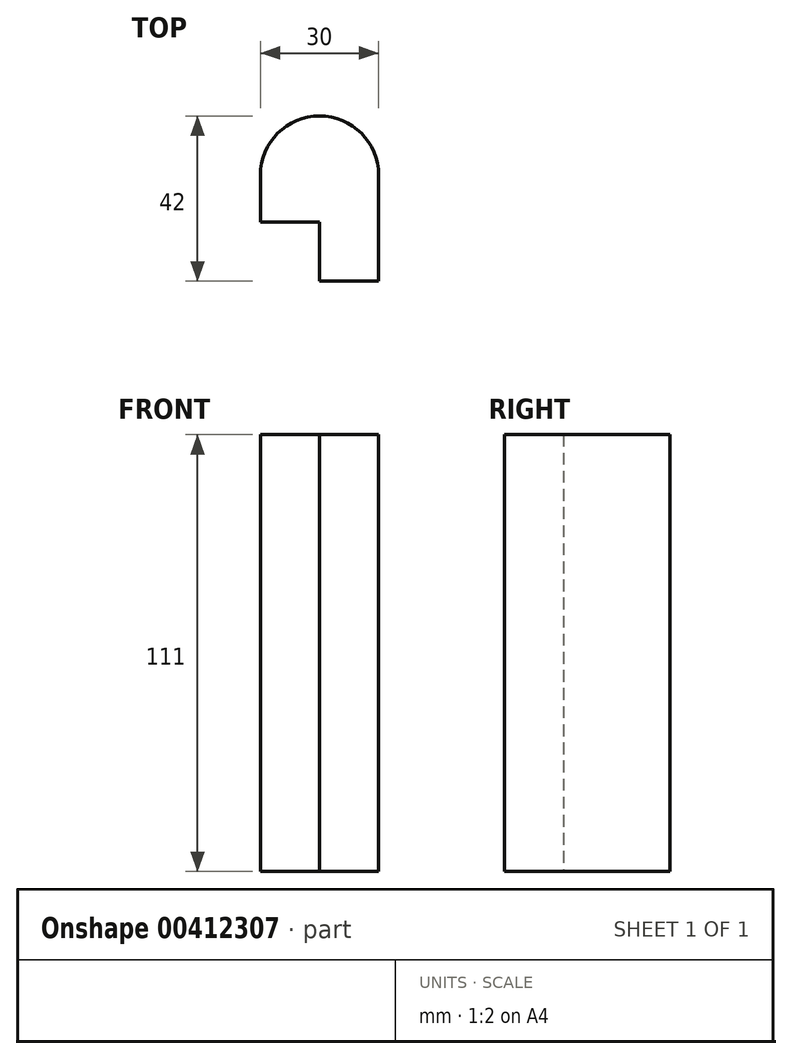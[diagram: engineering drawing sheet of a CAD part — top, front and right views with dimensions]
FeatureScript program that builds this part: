
annotation { "Feature Type Name" : "Feature", "Feature Type Description" : "" }
export const myFeature = defineFeature(function(context is Context, id is Id, definition is map)
    precondition{}
    {
        {
            var Q0;
            Q0=qCreatedBy(makeId("Top.planeOp"),FACE);
            var sketch = newSketch(context, id + "F0", { "sketchPlane" : qUnion([Q0])});
            skLineSegment(sketch, "E0", {"start": v(6.17, 0) * mm, "end": v(6.17, 15) * mm});
            skLineSegment(sketch, "E1", {"start": v(6.17, 15) * mm, "end": v(-8.83, 15) * mm});
            skLineSegment(sketch, "E2", {"start": v(-8.83, 15) * mm, "end": v(-8.83, 27) * mm});
            skLineSegment(sketch, "E3", {"start": v(-8.83, 27) * mm, "end": v(21.17, 27) * mm});
            skLineSegment(sketch, "E4", {"start": v(21.17, 27) * mm, "end": v(21.17, 0) * mm});
            skLineSegment(sketch, "E5", {"start": v(21.17, 0) * mm, "end": v(6.17, 0) * mm});
            skArc(sketch, "E6", {"start": v(21.17, 27) * mm, "mid": v(6.17, 42) * mm, "end": v(-8.83, 27) * mm});
            skSolve(sketch);
        }
        {
            var Q0;
            Q0 = qSketchRegion(id + "F0", true);
            extrude(context, id + "F1", {"entities" : qUnion([Q0]), "depth" : 111 * mm});
        }
    });
